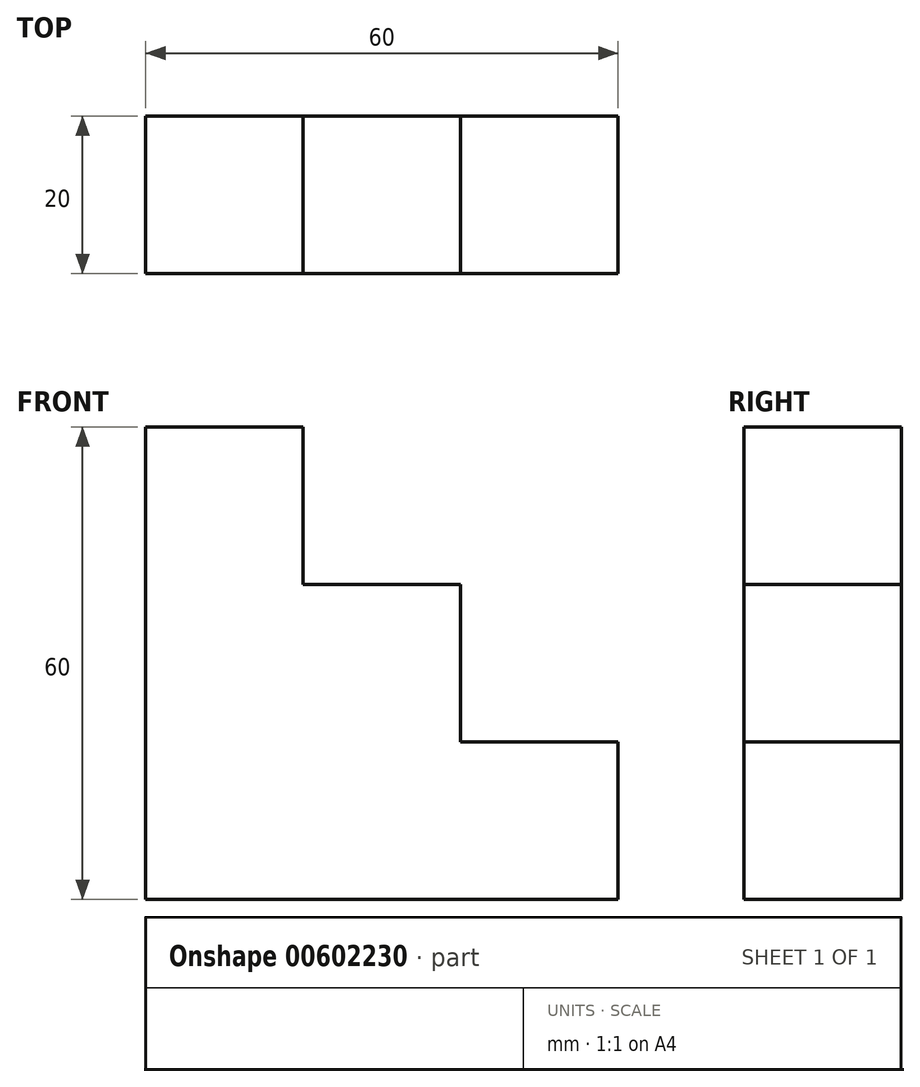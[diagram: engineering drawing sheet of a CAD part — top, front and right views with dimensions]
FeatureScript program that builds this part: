
annotation { "Feature Type Name" : "Feature", "Feature Type Description" : "" }
export const myFeature = defineFeature(function(context is Context, id is Id, definition is map)
    precondition{}
    {
        {
            var Q0;
            Q0=qCreatedBy(makeId("Front.planeOp"),FACE);
            var sketch = newSketch(context, id + "F0", { "sketchPlane" : qUnion([Q0])});
            skLineSegment(sketch, "E0", {"start": v(-45.02, 26.42) * mm, "end": v(-25.02, 26.42) * mm});
            skLineSegment(sketch, "E1", {"start": v(-25.02, 26.42) * mm, "end": v(-25.02, 6.42) * mm});
            skLineSegment(sketch, "E2", {"start": v(-25.02, 6.42) * mm, "end": v(-5.02, 6.42) * mm});
            skLineSegment(sketch, "E3", {"start": v(-5.02, 6.42) * mm, "end": v(-5.02, -13.58) * mm});
            skLineSegment(sketch, "E4", {"start": v(-5.02, -13.58) * mm, "end": v(14.98, -13.58) * mm});
            skLineSegment(sketch, "E5", {"start": v(14.98, -13.58) * mm, "end": v(14.98, -33.58) * mm});
            skLineSegment(sketch, "E6", {"start": v(14.98, -33.58) * mm, "end": v(-45.02, -33.58) * mm});
            skLineSegment(sketch, "E7", {"start": v(-45.02, -33.58) * mm, "end": v(-45.02, 26.42) * mm});
            skSolve(sketch);
        }
        {
            var Q0;
            Q0 = qSketchRegion(id + "F0", true);
            extrude(context, id + "F1", {"entities" : qUnion([Q0]), "depth" : 20 * mm, "offsetDistance" : 25 * mm});
        }
    });
